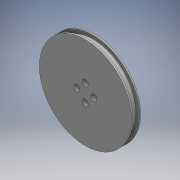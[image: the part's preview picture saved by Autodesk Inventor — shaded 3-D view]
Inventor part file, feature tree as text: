
AUTODESK INVENTOR PART (.ipt)
format: ipt  version: 2016 (Build 200138000, 138)  size: 134,144 bytes
history: native  units: mm
features: sketch x5, extrude x4, hole x1
ambient origin geometry x8: Origin, YZ Plane, XZ Plane, XY Plane, X Axis, Y Axis, Z Axis, Center Point
bodies: Solid1 (feature_tree)
feature tree (10):
  extrude  "Extrusion1"  Depth=1.0mm TaperAngle=0.0deg
  extrude  "Extrusion2"  Depth=4.5mm TaperAngle=0.0deg
  extrude  "Extrusion3"  Depth=1.0mm TaperAngle=0.0deg
  extrude  "Extrusion4"  Depth=1.5mm TaperAngle=0.0deg
  hole  "Hole1"  [1 undecoded]
  sketch  "Sketch1"  dims[d0=65.0mm d1=1.0mm d2=0.0mm]
  sketch  "Sketch2"  dims[d3=60.0mm d4=4.5mm d5=0.0mm]
  sketch  "Sketch3"  dims[d6=65.0mm d7=1.0mm d8=0.0mm]
  sketch  "Sketch4"  dims[d9=19.5mm d10=1.5mm d11=0.0mm]
  sketch  "Sketch5"  dims[d12=4.3mm d13=6.0mm d14=4.3mm d15=12.0mm d16=4.3mm d17=6.0mm d18=4.3mm d19=12.0mm d20=4.3mm d21=6.0mm d22=4.0mm d23=2.0mm d24=90.0deg d25=8.0mm d26=20.594885mm]
note: 1 required parameter value undecoded (feature->parameter linkage not recoverable at this tier; creation-order binding heuristic only, values carry confidence <= 0.55)
